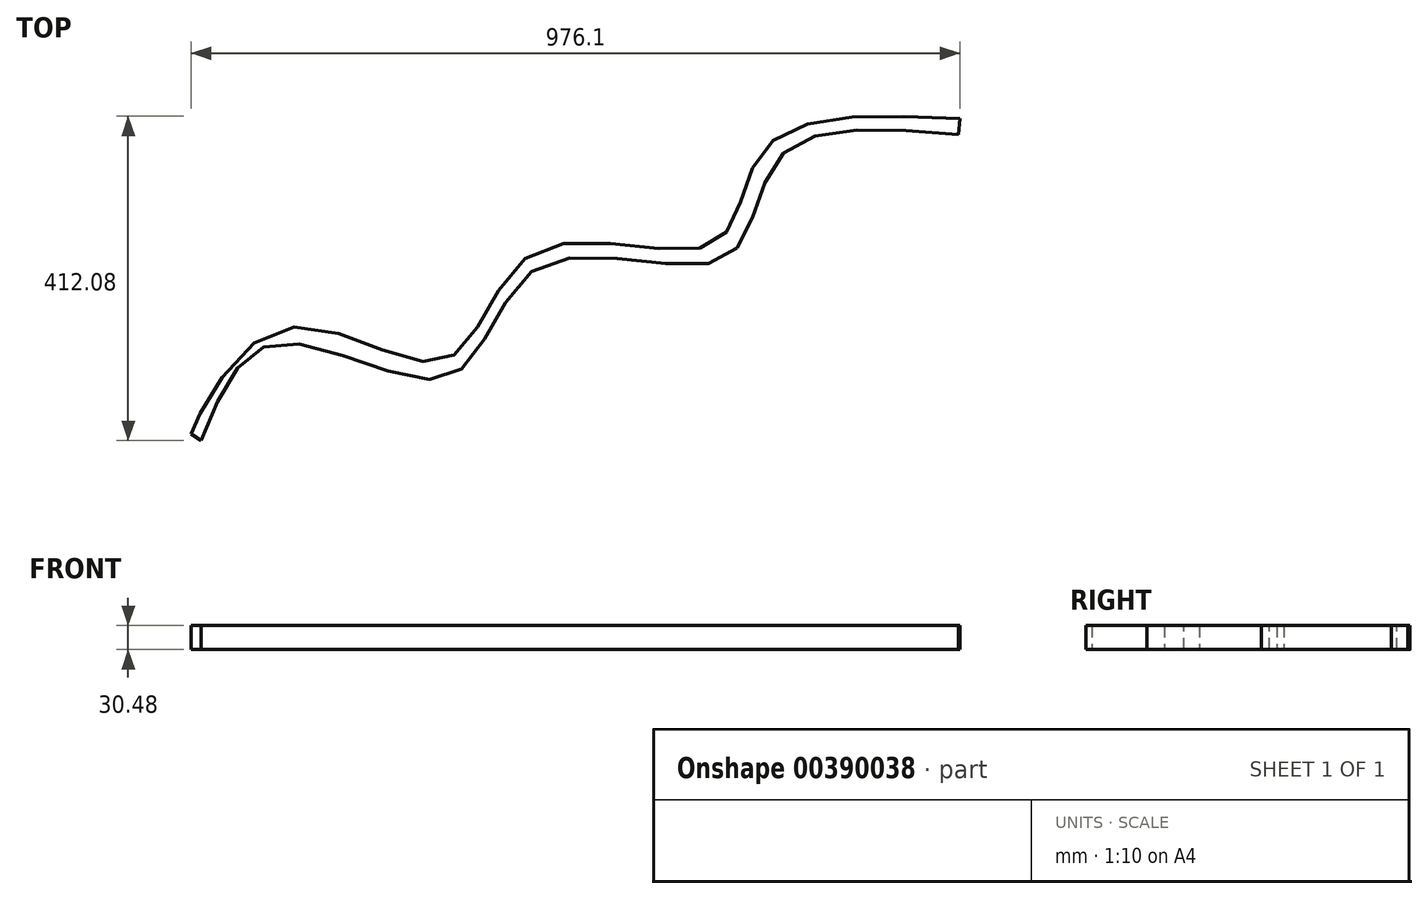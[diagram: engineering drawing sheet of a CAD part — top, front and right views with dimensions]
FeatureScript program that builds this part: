
annotation { "Feature Type Name" : "Feature", "Feature Type Description" : "" }
export const myFeature = defineFeature(function(context is Context, id is Id, definition is map)
    precondition{}
    {
        {
            var Q0;
            Q0=qCreatedBy(makeId("Top.planeOp"),FACE);
            var sketch = newSketch(context, id + "F0", { "sketchPlane" : qUnion([Q0])});
            skFitSpline(sketch, "E0", {"points": [v(481.5, 306.92) * mm, v(233.4, 268.75) * mm, v(169.32, 148.79) * mm, v(-56.98, 137.88) * mm, v(-174.22, 0) * mm, v(-385.53, 38.36) * mm, v(-494.6, -93.88) * mm, v(-494.6, -95.24) * mm], "startDerivative": vector(-1663.66, 80.95) * mm, "endDerivative": vector(24.4, -46.75) * mm});
            skFitSpline(sketch, "E1", {"points": [v(480.15, 286.48) * mm, v(252.48, 257.85) * mm, v(182.95, 129.7) * mm, v(-50.17, 120.16) * mm, v(-167.4, -20.26) * mm, v(-382.8, 22) * mm, v(-482.32, -102.06) * mm], "startDerivative": vector(-1551.58, 138.15) * mm, "endDerivative": vector(-472.06, -1180.03) * mm});
            skFitSpline(sketch, "E2", {"points": [v(-494.6, -93.88) * mm, v(-482.32, -102.06) * mm], "startDerivative": vector(12.27, -8.18) * mm, "endDerivative": vector(12.27, -8.18) * mm});
            skFitSpline(sketch, "E3", {"points": [v(481.5, 306.92) * mm, v(480.15, 286.48) * mm], "startDerivative": vector(-1.36, -20.45) * mm, "endDerivative": vector(-1.36, -20.45) * mm});
            skSolve(sketch);
        }
        {
            var Q0;
            Q0 = qSketchRegion(id + "F0", true);
            extrude(context, id + "F1", {"entities" : qUnion([Q0]), "depth" : 30.48 * mm});
        }
    });
